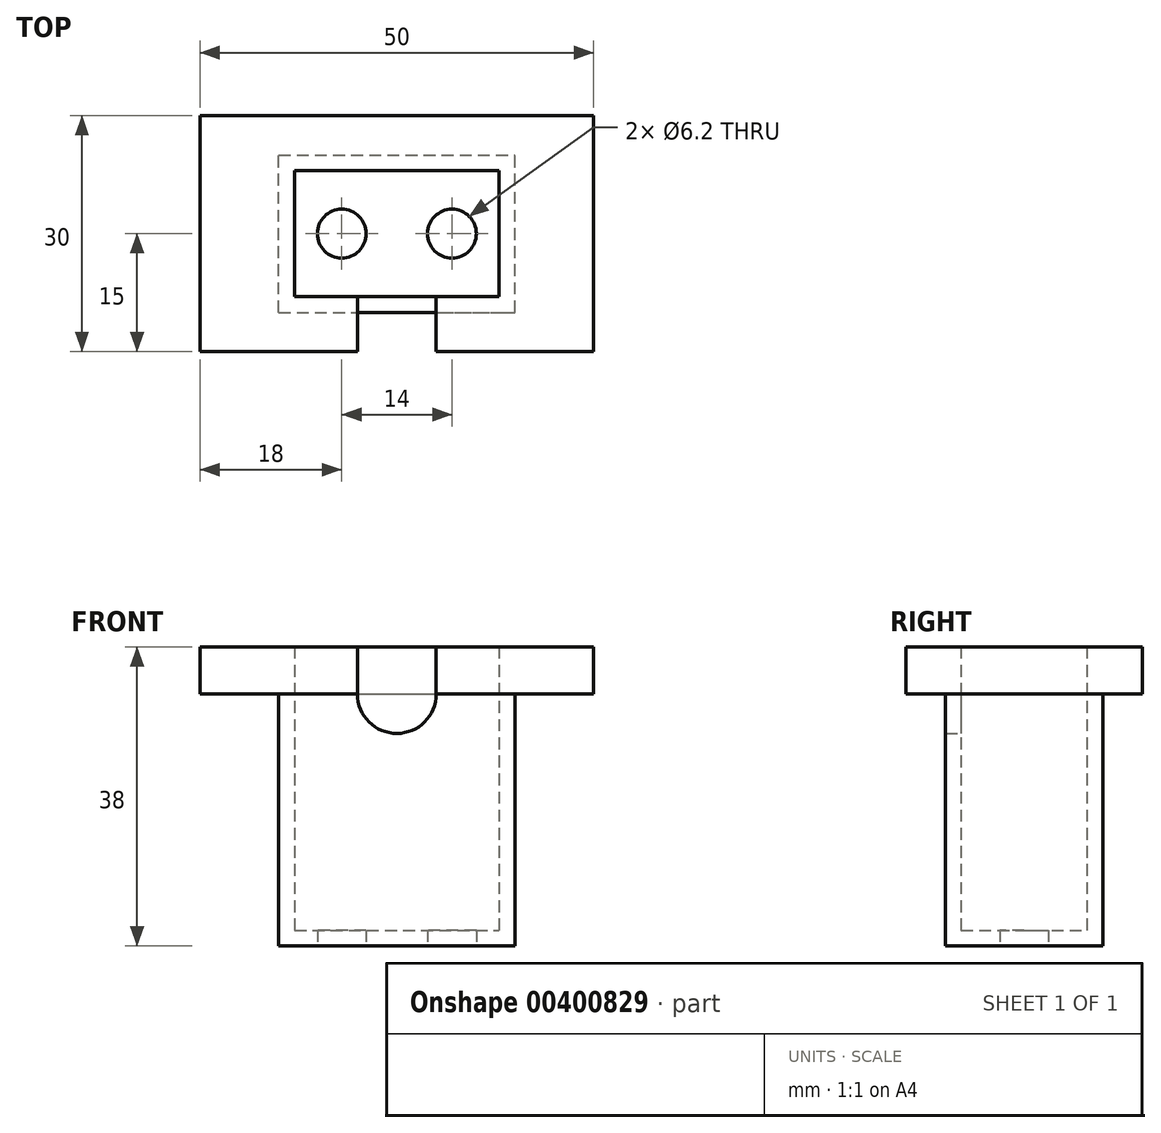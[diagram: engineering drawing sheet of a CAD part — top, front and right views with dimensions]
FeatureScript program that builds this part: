
annotation { "Feature Type Name" : "Feature", "Feature Type Description" : "" }
export const myFeature = defineFeature(function(context is Context, id is Id, definition is map)
    precondition{}
    {
        {
            var Q0;
            Q0=qCreatedBy(makeId("Top.planeOp"),FACE);
            var sketch = newSketch(context, id + "F0", { "sketchPlane" : qUnion([Q0])});
            skLineSegment(sketch, "E0.bottom", {"start": v(0, 0) * mm, "end": v(30, 0) * mm});
            skLineSegment(sketch, "E0.top", {"start": v(0, 20) * mm, "end": v(30, 20) * mm});
            skLineSegment(sketch, "E0.left", {"start": v(0, 0) * mm, "end": v(0, 20) * mm});
            skLineSegment(sketch, "E0.right", {"start": v(30, 0) * mm, "end": v(30, 20) * mm});
            skSolve(sketch);
        }
        {
            var Q0;
            Q0 = qSketchRegion(id + "F0", true);
            extrude(context, id + "F1", {"entities" : qUnion([Q0]), "depth" : 2 * mm});
        }
        {
            var Q0;
            Q0=makeQuery(id+"F1.opExtrude","CAP_FACE",FACE,{"disambiguationData":[OSD([sQuery(id+"F0.wireOp",EDGE,"E0.bottom"),sQuery(id+"F0.wireOp",EDGE,"E0.top"),sQuery(id+"F0.wireOp",EDGE,"E0.left"),sQuery(id+"F0.wireOp",EDGE,"E0.right")])],"isStart":false});
            var sketch = newSketch(context, id + "F2", { "sketchPlane" : qUnion([Q0])});
            skLineSegment(sketch, "E1.bottom", {"start": v(0, 0) * mm, "end": v(30, 0) * mm});
            skLineSegment(sketch, "E1.top", {"start": v(0, 20) * mm, "end": v(30, 20) * mm});
            skLineSegment(sketch, "E1.left", {"start": v(0, 0) * mm, "end": v(0, 20) * mm});
            skLineSegment(sketch, "E1.right", {"start": v(30, 0) * mm, "end": v(30, 20) * mm});
            skLineSegment(sketch, "E2.0", {"start": v(2, 18) * mm, "end": v(28, 18) * mm});
            skLineSegment(sketch, "E2.1", {"start": v(2, 2) * mm, "end": v(2, 18) * mm});
            skLineSegment(sketch, "E2.2", {"start": v(2, 2) * mm, "end": v(28, 2) * mm});
            skLineSegment(sketch, "E2.3", {"start": v(28, 2) * mm, "end": v(28, 18) * mm});
            skSolve(sketch);
        }
        {
            var Q0;
            Q0 = qSketchRegion(id + "F2", true);
            extrude(context, id + "F3", {"entities" : qUnion([Q0]), "operationType" : NewBodyOperationType.ADD, "depth" : 30 * mm});
        }
        {
            var Q0;
            Q0=makeQuery(id+"F1.opExtrude","CAP_FACE",FACE,{"disambiguationData":[OSD([sQuery(id+"F0.wireOp",EDGE,"E0.bottom"),sQuery(id+"F0.wireOp",EDGE,"E0.top"),sQuery(id+"F0.wireOp",EDGE,"E0.left"),sQuery(id+"F0.wireOp",EDGE,"E0.right")])],"isStart":true});
            var sketch = newSketch(context, id + "F4", { "sketchPlane" : qUnion([Q0])});
            skCircle(sketch, "E3", {"center": v(8, -10) * mm, "radius": 3.1 * mm});
            skCircle(sketch, "E4", {"center": v(22, -10) * mm, "radius": 3.1 * mm});
            skSolve(sketch);
        }
        {
            var Q0;
            Q0 = qSketchRegion(id + "F4", true);
            extrude(context, id + "F5", {"entities" : qUnion([Q0]), "operationType" : NewBodyOperationType.REMOVE, "oppositeDirection" : true, "depth" : 25 * mm});
        }
        {
            var Q0;
            Q0=makeQuery(id+"F3.opExtrude","CAP_FACE",FACE,{"disambiguationData":[OSD([sQuery(id+"F2.wireOp",EDGE,"E1.bottom"),sQuery(id+"F2.wireOp",EDGE,"E1.top"),sQuery(id+"F2.wireOp",EDGE,"E1.left"),sQuery(id+"F2.wireOp",EDGE,"E1.right"),sQuery(id+"F2.wireOp",EDGE,"E2.0"),sQuery(id+"F2.wireOp",EDGE,"E2.1"),sQuery(id+"F2.wireOp",EDGE,"E2.2"),sQuery(id+"F2.wireOp",EDGE,"E2.3")])],"isStart":false});
            var sketch = newSketch(context, id + "F6", { "sketchPlane" : qUnion([Q0])});
            skLineSegment(sketch, "E5.bottom", {"start": v(2, 2) * mm, "end": v(28, 2) * mm});
            skLineSegment(sketch, "E5.top", {"start": v(2, 18) * mm, "end": v(28, 18) * mm});
            skLineSegment(sketch, "E5.left", {"start": v(2, 2) * mm, "end": v(2, 18) * mm});
            skLineSegment(sketch, "E5.right", {"start": v(28, 2) * mm, "end": v(28, 18) * mm});
            skLineSegment(sketch, "E6.bottom", {"start": v(-10, -5) * mm, "end": v(40, -5) * mm});
            skLineSegment(sketch, "E6.top", {"start": v(-10, 25) * mm, "end": v(40, 25) * mm});
            skLineSegment(sketch, "E6.left", {"start": v(-10, -5) * mm, "end": v(-10, 25) * mm});
            skLineSegment(sketch, "E6.right", {"start": v(40, -5) * mm, "end": v(40, 25) * mm});
            skSolve(sketch);
        }
        {
            var Q0;
            Q0 = qSketchRegion(id + "F6", true);
            extrude(context, id + "F7", {"entities" : qUnion([Q0]), "operationType" : NewBodyOperationType.ADD, "depth" : 6 * mm});
        }
        {
            var Q0;
            Q0=makeQuery(id+"F7.boolean.opBoolean","MERGE",FACE,{"derivedFrom":[makeQuery(id+"F3.opExtrude","SWEPT_FACE",FACE,{"disambiguationData":[OSD([sQuery(id+"F2.wireOp",EDGE,"E2.2")])]}),makeQuery(id+"F7.opExtrude","SWEPT_FACE",FACE,{"disambiguationData":[OSD([sQuery(id+"F6.wireOp",EDGE,"E5.bottom")])]})]});
            var sketch = newSketch(context, id + "F8", { "sketchPlane" : qUnion([Q0])});
            skArc(sketch, "E7", {"start": v(-20, 32) * mm, "mid": v(-15, 27) * mm, "end": v(-10, 32) * mm});
            skLineSegment(sketch, "E8", {"start": v(-10, 38) * mm, "end": v(-10, 32) * mm});
            skLineSegment(sketch, "E9", {"start": v(-10, 38) * mm, "end": v(-20, 38) * mm});
            skLineSegment(sketch, "E10", {"start": v(-20, 38) * mm, "end": v(-20, 32) * mm});
            skSolve(sketch);
        }
        {
            var Q0;
            Q0 = qSketchRegion(id + "F8", true);
            extrude(context, id + "F9", {"entities" : qUnion([Q0]), "operationType" : NewBodyOperationType.REMOVE, "oppositeDirection" : true, "depth" : 25 * mm});
        }
    });
